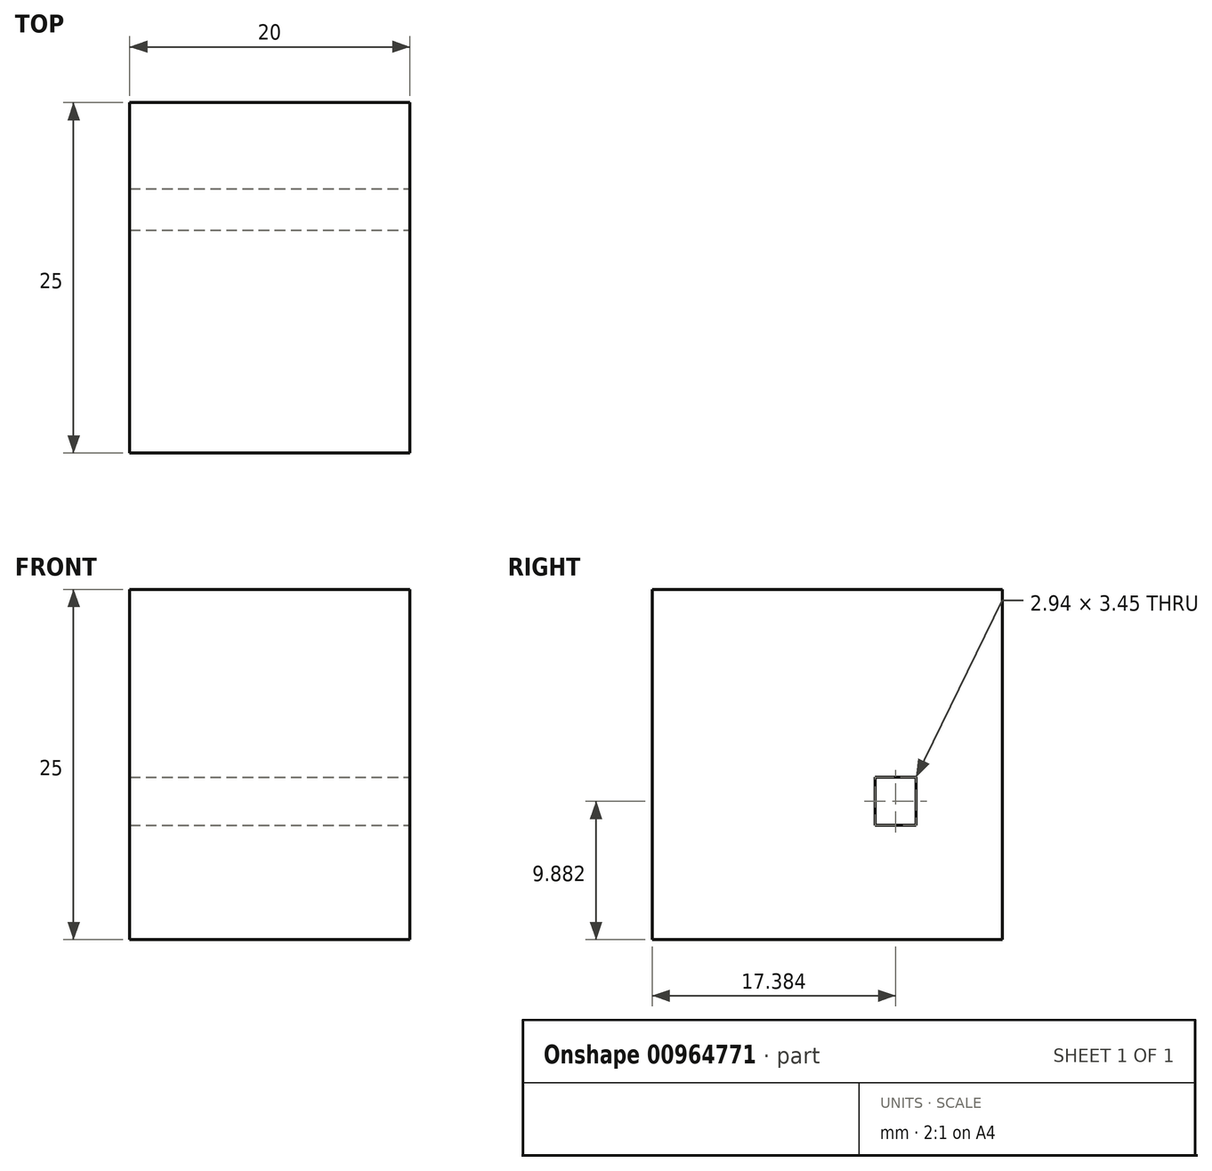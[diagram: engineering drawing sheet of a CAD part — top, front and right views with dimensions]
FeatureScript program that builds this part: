
annotation { "Feature Type Name" : "Feature", "Feature Type Description" : "" }
export const myFeature = defineFeature(function(context is Context, id is Id, definition is map)
    precondition{}
    {
        {
            var Q0;
            Q0=qCreatedBy(makeId("Top.planeOp"),FACE);
            var sketch = newSketch(context, id + "F0", { "sketchPlane" : qUnion([Q0])});
            skLineSegment(sketch, "E0.bottom", {"start": v(0, 25) * mm, "end": v(20, 25) * mm});
            skLineSegment(sketch, "E0.top", {"start": v(0, 0) * mm, "end": v(20, 0) * mm});
            skLineSegment(sketch, "E0.left", {"start": v(0, 25) * mm, "end": v(0, 0) * mm});
            skLineSegment(sketch, "E0.right", {"start": v(20, 25) * mm, "end": v(20, 0) * mm});
            skSolve(sketch);
        }
        {
            var Q0;
            Q0 = qSketchRegion(id + "F0", true);
            extrude(context, id + "F1", {"entities" : qUnion([Q0]), "depth" : 25 * mm, "offsetDistance" : 25 * mm, "symmetric" : true});
        }
        {
            var Q0;
            Q0=makeQuery(id+"F1.opExtrude","SWEPT_FACE",FACE,{"disambiguationData":[OSD([sQuery(id+"F0.wireOp",EDGE,"E0.right")])]});
            var sketch = newSketch(context, id + "F2", { "sketchPlane" : qUnion([Q0])});
            skCircle(sketch, "E1", {"center": v(10, 2.5) * mm, "radius": 5 * mm});
            skSolve(sketch);
        }
        {
            var Q0;
            Q0=makeQuery(id+"F2.imprint","IMPRINT",FACE,{"disambiguationData":[TD([[makeQuery(id+"F2.imprint","IMPRINT",EDGE,{"derivedFrom":sQuery(id+"F2.wireOp",EDGE,"E1")}),-1.0]])]});
            var sketch = newSketch(context, id + "F3", { "sketchPlane" : qUnion([Q0])});
            skLineSegment(sketch, "E2.bottom", {"start": v(18.85, -0.9) * mm, "end": v(15.92, -0.9) * mm});
            skLineSegment(sketch, "E2.top", {"start": v(18.85, -4.34) * mm, "end": v(15.92, -4.34) * mm});
            skLineSegment(sketch, "E2.left", {"start": v(18.85, -0.9) * mm, "end": v(18.85, -4.34) * mm});
            skLineSegment(sketch, "E2.right", {"start": v(15.92, -0.9) * mm, "end": v(15.92, -4.34) * mm});
            skSolve(sketch);
        }
        {
            var Q0;
            Q0 = qSketchRegion(id + "F3", true);
            extrude(context, id + "F4", {"entities" : qUnion([Q0]), "operationType" : NewBodyOperationType.REMOVE, "oppositeDirection" : true, "depth" : 25 * mm, "offsetDistance" : 25 * mm});
        }
    });
